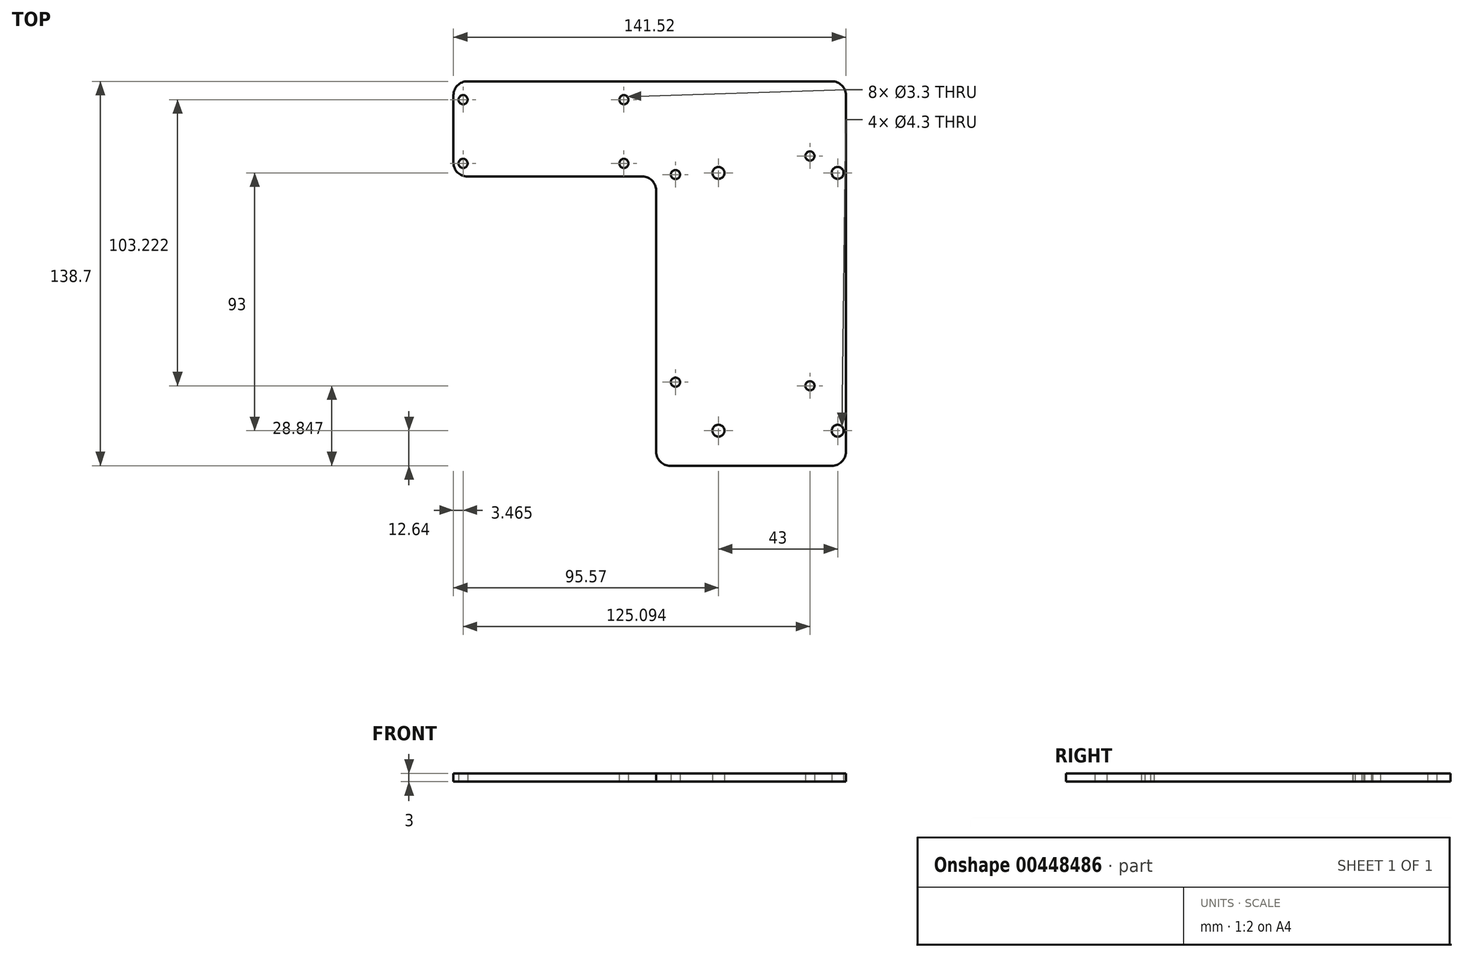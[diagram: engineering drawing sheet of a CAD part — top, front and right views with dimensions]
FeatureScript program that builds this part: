
annotation { "Feature Type Name" : "Feature", "Feature Type Description" : "" }
export const myFeature = defineFeature(function(context is Context, id is Id, definition is map)
    precondition{}
    {
        {
            var Q0;
            Q0=qCreatedBy(makeId("Top.planeOp"),FACE);
            var sketch = newSketch(context, id + "F0", { "sketchPlane" : qUnion([Q0])});
            skLineSegment(sketch, "E0.bottom", {"start": v(-21.5, 46.5) * mm, "end": v(21.5, 46.5) * mm, "construction": true});
            skLineSegment(sketch, "E0.top", {"start": v(-21.5, -46.5) * mm, "end": v(21.5, -46.5) * mm, "construction": true});
            skLineSegment(sketch, "E0.left", {"start": v(-21.5, 46.5) * mm, "end": v(-21.5, -46.5) * mm, "construction": true});
            skLineSegment(sketch, "E0.right", {"start": v(21.5, 46.5) * mm, "end": v(21.5, -46.5) * mm, "construction": true});
            skPoint(sketch, "E0.middle", {"position": v(0, 0) * mm});
            skLineSegment(sketch, "E1.bottom", {"start": v(24.45, -59.14) * mm, "end": v(-43.95, -59.14) * mm});
            skLineSegment(sketch, "E1.top", {"start": v(24.45, 79.56) * mm, "end": v(-117.07, 79.56) * mm});
            skLineSegment(sketch, "E1.left", {"start": v(24.45, -59.14) * mm, "end": v(24.45, 79.56) * mm});
            skLineSegment(sketch, "E1.right", {"start": v(-117.07, 45.2) * mm, "end": v(-117.07, 79.56) * mm});
            skLineSegment(sketch, "E2.bottom", {"start": v(-55.6, 49.93) * mm, "end": v(-113.6, 49.93) * mm, "construction": true});
            skLineSegment(sketch, "E2.top", {"start": v(-55.6, 72.93) * mm, "end": v(-113.6, 72.93) * mm, "construction": true});
            skLineSegment(sketch, "E2.left", {"start": v(-55.6, 49.93) * mm, "end": v(-55.6, 72.93) * mm, "construction": true});
            skLineSegment(sketch, "E2.right", {"start": v(-113.6, 49.93) * mm, "end": v(-113.6, 72.93) * mm, "construction": true});
            skLineSegment(sketch, "E3", {"start": v(-43.95, 45.2) * mm, "end": v(-43.95, -59.14) * mm});
            skLineSegment(sketch, "E4", {"start": v(-43.95, 45.2) * mm, "end": v(-117.07, 45.2) * mm});
            skPoint(sketch, "E5.orphan", {"position": v(-96.4, 75.9) * mm});
            skLineSegment(sketch, "E6", {"start": v(-37.01, 45.9) * mm, "end": v(-37.01, -29) * mm, "construction": true});
            skLineSegment(sketch, "E7", {"start": v(11.49, 52.6) * mm, "end": v(11.49, -30.3) * mm, "construction": true});
            skLineSegment(sketch, "E8", {"start": v(15.34, -29) * mm, "end": v(117.39, -29) * mm, "construction": true});
            skSolve(sketch);
        }
        {
            var Q0;
            Q0=qSketchRegion(id+"F0",true);
            extrude(context, id + "F1", {"entities" : qUnion([Q0]), "depth" : 3 * mm, "offsetDistance" : 25 * mm});
        }
        {
            var Q0;
            Q0=sQuery(id+"F0.wireOp",VERTEX,"E2.top.end");
            var Q1;
            Q1=sQuery(id+"F0.wireOp",VERTEX,"E2.bottom.end");
            var Q2;
            Q2=sQuery(id+"F0.wireOp",VERTEX,"E2.bottom.start");
            var Q3;
            Q3=sQuery(id+"F0.wireOp",VERTEX,"E2.left.end");
            var Q4;
            Q4=sQuery(id+"F0.wireOp",VERTEX,"4N1vUwWh-xHJR-HAm5-r41G-x5FdNC7RSBuu.right.end");
            var Q5;
            Q5=sQuery(id+"F0.wireOp",VERTEX,"4N1vUwWh-xHJR-HAm5-r41G-x5FdNC7RSBuu.top.start");
            var Q6;
            Q6=sQuery(id+"F0.wireOp",VERTEX,"4N1vUwWh-xHJR-HAm5-r41G-x5FdNC7RSBuu.right.start");
            var Q7;
            Q7=sQuery(id+"F0.wireOp",VERTEX,"4N1vUwWh-xHJR-HAm5-r41G-x5FdNC7RSBuu.bottom.start");
            var Q8;
            Q8=sQuery(id+"F0.wireOp",VERTEX,"E6.start");
            var Q9;
            Q9=sQuery(id+"F0.wireOp",VERTEX,"E7.start");
            var Q10;
            Q10=sQuery(id+"F0.wireOp",VERTEX,"E7.end");
            var Q11;
            Q11=sQuery(id+"F0.wireOp",VERTEX,"E6.end");
            var Q12;
            Q12=makeQuery(id+"F1.opExtrude","SWEPT_BODY",BODY,{"disambiguationData":[OSD([sQuery(id+"F0.wireOp",EDGE,"E1.bottom"),sQuery(id+"F0.wireOp",EDGE,"E1.top"),sQuery(id+"F0.wireOp",EDGE,"E1.left"),sQuery(id+"F0.wireOp",EDGE,"E1.right"),sQuery(id+"F0.wireOp",EDGE,"E3"),sQuery(id+"F0.wireOp",EDGE,"XyIVaQW3-El7N-e6bz-1eAk-mJc9jGYG2OAW"),sQuery(id+"F0.wireOp",EDGE,"2inYUX5w-coaZ-2hAe-3aFK-Vs1NiTnumc5f"),sQuery(id+"F0.wireOp",EDGE,"E4")])]});
            hole(context, id + "F2", {"style" : HoleStyle.SIMPLE, "endStyle" : HoleEndStyle.THROUGH, "oppositeDirection" : true, "standardTappedOrClearance" : lookupTablePath({ "standard" : "ISO", "fit" : "Normal", "size" : "M3", "type" : "Clearance" }), "standardBlindInLast" : lookupTablePath({ "fit" : "Standard", "standard" : "ISO", "size" : "M3", "type" : "Clearance" }), "holeDiameter" : 3.3 * mm, "majorDiameter" : 5 * mm, "isTappedThrough" : true, "tappedDepth" : 12 * mm, "tapClearance" : 3, "startFromSketch" : true, "locations" : qUnion([Q0, Q1, Q2, Q3, Q4, Q5, Q6, Q7, Q8, Q9, Q10, Q11]), "scope" : qUnion([Q12])});
        }
        {
            var Q0;
            Q0=sQuery(id+"F0.wireOp",VERTEX,"E0.left.start");
            var Q1;
            Q1=sQuery(id+"F0.wireOp",VERTEX,"E0.right.start");
            var Q2;
            Q2=sQuery(id+"F0.wireOp",VERTEX,"E0.right.end");
            var Q3;
            Q3=sQuery(id+"F0.wireOp",VERTEX,"E0.left.end");
            var Q4;
            Q4=makeQuery(id+"F1.opExtrude","SWEPT_BODY",BODY,{"disambiguationData":[OSD([sQuery(id+"F0.wireOp",EDGE,"E1.bottom"),sQuery(id+"F0.wireOp",EDGE,"E1.top"),sQuery(id+"F0.wireOp",EDGE,"E1.left"),sQuery(id+"F0.wireOp",EDGE,"E1.right"),sQuery(id+"F0.wireOp",EDGE,"E3"),sQuery(id+"F0.wireOp",EDGE,"XyIVaQW3-El7N-e6bz-1eAk-mJc9jGYG2OAW"),sQuery(id+"F0.wireOp",EDGE,"2inYUX5w-coaZ-2hAe-3aFK-Vs1NiTnumc5f"),sQuery(id+"F0.wireOp",EDGE,"E4")])]});
            hole(context, id + "F3", {"style" : HoleStyle.SIMPLE, "endStyle" : HoleEndStyle.THROUGH, "oppositeDirection" : true, "holeDiameter" : 4.3 * mm, "majorDiameter" : 5 * mm, "isTappedThrough" : true, "tappedDepth" : 12 * mm, "tapClearance" : 3, "startFromSketch" : true, "locations" : qUnion([Q0, Q1, Q2, Q3]), "scope" : qUnion([Q4])});
        }
        {
            var Q0;
            Q0=makeQuery(id+"F1.opExtrude","SWEPT_EDGE",EDGE,{"disambiguationData":[OSD([sQuery(id+"F0.wireOp",EDGE,"E1.top"),sQuery(id+"F0.wireOp",EDGE,"E1.right")])]});
            var Q1;
            Q1=makeQuery(id+"F1.opExtrude","SWEPT_EDGE",EDGE,{"disambiguationData":[OSD([sQuery(id+"F0.wireOp",EDGE,"XyIVaQW3-El7N-e6bz-1eAk-mJc9jGYG2OAW"),sQuery(id+"F0.wireOp",EDGE,"2inYUX5w-coaZ-2hAe-3aFK-Vs1NiTnumc5f")])]});
            var Q2;
            Q2=makeQuery(id+"F1.opExtrude","SWEPT_EDGE",EDGE,{"disambiguationData":[OSD([sQuery(id+"F0.wireOp",EDGE,"E3"),sQuery(id+"F0.wireOp",EDGE,"XyIVaQW3-El7N-e6bz-1eAk-mJc9jGYG2OAW")])]});
            var Q3;
            Q3=makeQuery(id+"F1.opExtrude","SWEPT_EDGE",EDGE,{"disambiguationData":[OSD([sQuery(id+"F0.wireOp",EDGE,"E3"),sQuery(id+"F0.wireOp",EDGE,"E4")])]});
            var Q4;
            Q4=makeQuery(id+"F1.opExtrude","SWEPT_EDGE",EDGE,{"disambiguationData":[OSD([sQuery(id+"F0.wireOp",EDGE,"E1.bottom"),sQuery(id+"F0.wireOp",EDGE,"2inYUX5w-coaZ-2hAe-3aFK-Vs1NiTnumc5f")])]});
            var Q5;
            Q5=makeQuery(id+"F1.opExtrude","SWEPT_EDGE",EDGE,{"disambiguationData":[OSD([sQuery(id+"F0.wireOp",EDGE,"E1.right"),sQuery(id+"F0.wireOp",EDGE,"E4")])]});
            var Q6;
            Q6=makeQuery(id+"F1.opExtrude","SWEPT_EDGE",EDGE,{"disambiguationData":[OSD([sQuery(id+"F0.wireOp",EDGE,"E1.top"),sQuery(id+"F0.wireOp",EDGE,"E1.left")])]});
            var Q7;
            Q7=makeQuery(id+"F1.opExtrude","SWEPT_EDGE",EDGE,{"disambiguationData":[OSD([sQuery(id+"F0.wireOp",EDGE,"E1.bottom"),sQuery(id+"F0.wireOp",EDGE,"E1.left")])]});
            var Q8;
            Q8=makeQuery(id+"F1.opExtrude","SWEPT_EDGE",EDGE,{"disambiguationData":[OSD([sQuery(id+"F0.wireOp",EDGE,"Mbf7E7DW-qALH-cvkv-Damv-hvnqM2JEZsVI"),sQuery(id+"F0.wireOp",EDGE,"yL2UZmJc-QStA-b8Vo-1v86-bxjpKFNwprbL")])]});
            var Q9;
            Q9=makeQuery(id+"F1.opExtrude","SWEPT_EDGE",EDGE,{"disambiguationData":[OSD([sQuery(id+"F0.wireOp",EDGE,"qiIUHCKB-fCWY-SWhl-cjjz-M1Dty9vsqyQJ"),sQuery(id+"F0.wireOp",EDGE,"Q55u8Cbf-FWXE-ZP9w-DCtp-IPOpDFhRQxLW")])]});
            var Q10;
            Q10=makeQuery(id+"F1.opExtrude","SWEPT_EDGE",EDGE,{"disambiguationData":[OSD([sQuery(id+"F0.wireOp",EDGE,"a1f7CNFQ-nP29-92E3-ja6P-g6eo9MA6HpaG"),sQuery(id+"F0.wireOp",EDGE,"OeeX4dYa-ce1g-dk9C-RiQx-GZsGsBV5ChxM")])]});
            var Q11;
            Q11=makeQuery(id+"F1.opExtrude","SWEPT_EDGE",EDGE,{"disambiguationData":[OSD([sQuery(id+"F0.wireOp",EDGE,"OeeX4dYa-ce1g-dk9C-RiQx-GZsGsBV5ChxM"),sQuery(id+"F0.wireOp",EDGE,"j85sN3cy-DIR5-E17b-kCIM-lPXGn6SRW4FC")])]});
            var Q12;
            Q12=makeQuery(id+"F1.opExtrude","SWEPT_EDGE",EDGE,{"disambiguationData":[OSD([sQuery(id+"F0.wireOp",EDGE,"H5cnSjnK-4Nrg-yr1O-NTxU-GIKtI7yp09dG"),sQuery(id+"F0.wireOp",EDGE,"aUoxsp5O-AR9o-Et6y-4KpD-5wgRAlL37lOh")])]});
            var Q13;
            Q13=makeQuery(id+"F1.opExtrude","SWEPT_EDGE",EDGE,{"disambiguationData":[OSD([sQuery(id+"F0.wireOp",EDGE,"9UlV4Nop-iNJr-02NP-fapv-DWM8Iypxcy4n"),sQuery(id+"F0.wireOp",EDGE,"RAkMmiOb-nROR-mXBJ-D0fB-59uvw5uzIgUD")])]});
            var Q14;
            Q14=makeQuery(id+"F1.opExtrude","SWEPT_EDGE",EDGE,{"disambiguationData":[OSD([sQuery(id+"F0.wireOp",EDGE,"RpWV4TA2-qZx3-hfFS-Fjk5-bPTjN17klhtH"),sQuery(id+"F0.wireOp",EDGE,"2l11ivdO-LSoy-1MMf-z1oK-tAifx8Baqm9W")])]});
            fillet(context, id + "F4", {"entities" : qUnion([Q0, Q1, Q2, Q3, Q4, Q5, Q6, Q7, Q8, Q9, Q10, Q11, Q12, Q13, Q14]), "radius" : 5 * mm, "tangentPropagation" : true, "allowEdgeOverflow" : false});
        }
    });
